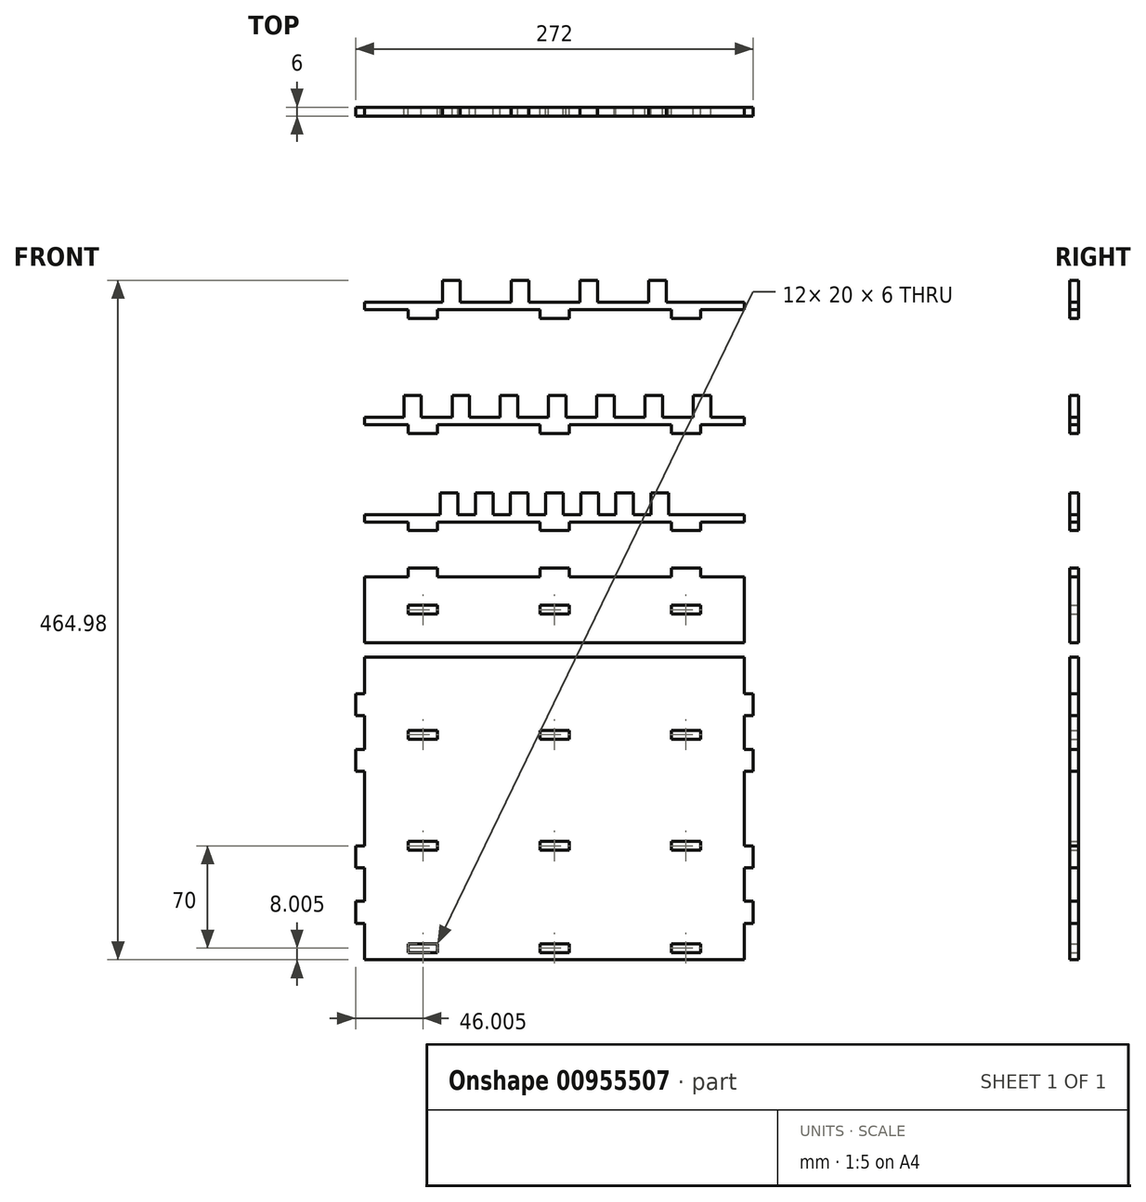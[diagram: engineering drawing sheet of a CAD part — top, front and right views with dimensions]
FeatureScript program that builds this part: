
annotation { "Feature Type Name" : "Feature", "Feature Type Description" : "" }
export const myFeature = defineFeature(function(context is Context, id is Id, definition is map)
    precondition{}
    {
        {
            var Q0;
            Q0=qCreatedBy(makeId("Front.planeOp"),FACE);
            var sketch = newSketch(context, id + "F0", { "sketchPlane" : qUnion([Q0])});
            skLineSegment(sketch, "E0", {"start": v(-47.37, 102.67) * mm, "end": v(-47.37, 117.67) * mm});
            skLineSegment(sketch, "E1", {"start": v(-47.37, 117.67) * mm, "end": v(-35.37, 117.67) * mm});
            skLineSegment(sketch, "E2", {"start": v(-35.37, 117.67) * mm, "end": v(-35.37, 102.67) * mm});
            skLineSegment(sketch, "E3", {"start": v(-35.37, 102.67) * mm, "end": v(-0.37, 102.67) * mm});
            skLineSegment(sketch, "E4.1.0.0", {"start": v(-0.37, 102.67) * mm, "end": v(-0.37, 117.67) * mm});
            skLineSegment(sketch, "E4.1.0.1", {"start": v(-0.37, 117.67) * mm, "end": v(11.63, 117.67) * mm});
            skLineSegment(sketch, "E4.1.0.2", {"start": v(11.63, 117.67) * mm, "end": v(11.63, 102.67) * mm});
            skLineSegment(sketch, "E4.1.0.3", {"start": v(11.63, 102.67) * mm, "end": v(46.63, 102.67) * mm});
            skLineSegment(sketch, "E4.2.0.0", {"start": v(46.63, 102.67) * mm, "end": v(46.63, 117.67) * mm});
            skLineSegment(sketch, "E4.2.0.1", {"start": v(46.63, 117.67) * mm, "end": v(58.63, 117.67) * mm});
            skLineSegment(sketch, "E4.2.0.2", {"start": v(58.63, 117.67) * mm, "end": v(58.63, 102.67) * mm});
            skLineSegment(sketch, "E4.2.0.3", {"start": v(58.63, 102.67) * mm, "end": v(93.63, 102.67) * mm});
            skLineSegment(sketch, "E4.3.0.0", {"start": v(93.63, 102.67) * mm, "end": v(93.63, 117.67) * mm});
            skLineSegment(sketch, "E4.3.0.1", {"start": v(93.63, 117.67) * mm, "end": v(105.63, 117.67) * mm});
            skLineSegment(sketch, "E4.3.0.2", {"start": v(105.63, 117.67) * mm, "end": v(105.63, 102.67) * mm});
            skLineSegment(sketch, "E4.direction1", {"start": v(-47.37, 102.67) * mm, "end": v(-0.37, 102.67) * mm, "construction": true});
            skLineSegment(sketch, "E5", {"start": v(-73.87, 23.95) * mm, "end": v(-73.87, 38.95) * mm});
            skLineSegment(sketch, "E6", {"start": v(-73.87, 38.95) * mm, "end": v(-61.87, 38.95) * mm});
            skLineSegment(sketch, "E7", {"start": v(-61.87, 38.95) * mm, "end": v(-61.87, 23.95) * mm});
            skLineSegment(sketch, "E8", {"start": v(-61.87, 23.95) * mm, "end": v(-40.87, 23.95) * mm});
            skLineSegment(sketch, "E9.1.0.0", {"start": v(-40.87, 23.95) * mm, "end": v(-40.87, 38.95) * mm});
            skLineSegment(sketch, "E9.1.0.1", {"start": v(-40.87, 38.95) * mm, "end": v(-28.87, 38.95) * mm});
            skLineSegment(sketch, "E9.1.0.2", {"start": v(-28.87, 38.95) * mm, "end": v(-28.87, 23.95) * mm});
            skLineSegment(sketch, "E9.1.0.3", {"start": v(-28.87, 23.95) * mm, "end": v(-7.87, 23.95) * mm});
            skLineSegment(sketch, "E9.2.0.0", {"start": v(-7.87, 23.95) * mm, "end": v(-7.87, 38.95) * mm});
            skLineSegment(sketch, "E9.2.0.1", {"start": v(-7.87, 38.95) * mm, "end": v(4.13, 38.95) * mm});
            skLineSegment(sketch, "E9.2.0.2", {"start": v(4.13, 38.95) * mm, "end": v(4.13, 23.95) * mm});
            skLineSegment(sketch, "E9.2.0.3", {"start": v(4.13, 23.95) * mm, "end": v(25.13, 23.95) * mm});
            skLineSegment(sketch, "E9.direction1", {"start": v(-73.87, 23.95) * mm, "end": v(-40.87, 23.95) * mm, "construction": true});
            skLineSegment(sketch, "E10", {"start": v(-47.37, 102.67) * mm, "end": v(-100.87, 102.67) * mm});
            skLineSegment(sketch, "E11", {"start": v(-100.87, 102.67) * mm, "end": v(-100.87, 97.67) * mm});
            skLineSegment(sketch, "E12", {"start": v(-100.87, 97.67) * mm, "end": v(-70.87, 97.67) * mm});
            skLineSegment(sketch, "E13", {"start": v(-73.87, 23.95) * mm, "end": v(-100.87, 23.95) * mm});
            skLineSegment(sketch, "E14", {"start": v(-100.87, 23.95) * mm, "end": v(-100.87, 18.95) * mm});
            skLineSegment(sketch, "E15", {"start": v(-100.87, 18.95) * mm, "end": v(-70.87, 18.95) * mm});
            skLineSegment(sketch, "E16.top", {"start": v(-70.87, 91.67) * mm, "end": v(-50.87, 91.67) * mm});
            skLineSegment(sketch, "E16.left", {"start": v(-70.87, 97.67) * mm, "end": v(-70.87, 91.67) * mm});
            skLineSegment(sketch, "E16.right", {"start": v(-50.87, 97.67) * mm, "end": v(-50.87, 91.67) * mm});
            skLineSegment(sketch, "E17.top", {"start": v(-70.87, 12.95) * mm, "end": v(-50.87, 12.95) * mm});
            skLineSegment(sketch, "E17.left", {"start": v(-70.87, 18.95) * mm, "end": v(-70.87, 12.95) * mm});
            skLineSegment(sketch, "E17.right", {"start": v(-50.87, 18.95) * mm, "end": v(-50.87, 12.95) * mm});
            skLineSegment(sketch, "E18.1.0.0", {"start": v(19.13, 97.67) * mm, "end": v(19.13, 91.67) * mm});
            skLineSegment(sketch, "E18.1.0.1", {"start": v(19.13, 91.67) * mm, "end": v(39.13, 91.67) * mm});
            skLineSegment(sketch, "E18.1.0.2", {"start": v(39.13, 97.67) * mm, "end": v(39.13, 91.67) * mm});
            skLineSegment(sketch, "E18.2.0.0", {"start": v(109.13, 97.67) * mm, "end": v(109.13, 91.67) * mm});
            skLineSegment(sketch, "E18.2.0.1", {"start": v(109.13, 91.67) * mm, "end": v(129.13, 91.67) * mm});
            skLineSegment(sketch, "E18.2.0.2", {"start": v(129.13, 97.67) * mm, "end": v(129.13, 91.67) * mm});
            skLineSegment(sketch, "E18.direction1", {"start": v(-70.87, 91.67) * mm, "end": v(19.13, 91.67) * mm, "construction": true});
            skLineSegment(sketch, "E19.1.0.0", {"start": v(19.13, 18.95) * mm, "end": v(19.13, 12.95) * mm});
            skLineSegment(sketch, "E19.1.0.1", {"start": v(19.13, 12.95) * mm, "end": v(39.13, 12.95) * mm});
            skLineSegment(sketch, "E19.1.0.2", {"start": v(39.13, 18.95) * mm, "end": v(39.13, 12.95) * mm});
            skLineSegment(sketch, "E19.2.0.0", {"start": v(109.13, 18.95) * mm, "end": v(109.13, 12.95) * mm});
            skLineSegment(sketch, "E19.2.0.1", {"start": v(109.13, 12.95) * mm, "end": v(129.13, 12.95) * mm});
            skLineSegment(sketch, "E19.2.0.2", {"start": v(129.13, 18.95) * mm, "end": v(129.13, 12.95) * mm});
            skLineSegment(sketch, "E19.direction1", {"start": v(-70.87, 12.95) * mm, "end": v(19.13, 12.95) * mm, "construction": true});
            skLineSegment(sketch, "E20.trimOffspring", {"start": v(-50.87, 97.67) * mm, "end": v(19.13, 97.67) * mm});
            skLineSegment(sketch, "E21.trimOffspring", {"start": v(39.13, 97.67) * mm, "end": v(109.13, 97.67) * mm});
            skLineSegment(sketch, "E22.trimOffspring", {"start": v(39.13, 18.95) * mm, "end": v(109.13, 18.95) * mm});
            skLineSegment(sketch, "E23.trimOffspring", {"start": v(-50.87, 18.95) * mm, "end": v(19.13, 18.95) * mm});
            skLineSegment(sketch, "E24.bottom", {"start": v(-100.87, -85.27) * mm, "end": v(-70.87, -85.27) * mm});
            skLineSegment(sketch, "E24.top", {"start": v(-100.87, -130.27) * mm, "end": v(159.13, -130.27) * mm});
            skLineSegment(sketch, "E24.left", {"start": v(-100.87, -85.27) * mm, "end": v(-100.87, -130.27) * mm});
            skLineSegment(sketch, "E24.right", {"start": v(159.13, -85.27) * mm, "end": v(159.13, -130.27) * mm});
            skLineSegment(sketch, "E25", {"start": v(-100.87, -107.77) * mm, "end": v(159.13, -107.77) * mm, "construction": true});
            skLineSegment(sketch, "E26.bottom", {"start": v(-70.87, -104.77) * mm, "end": v(-50.87, -104.77) * mm});
            skLineSegment(sketch, "E26.top", {"start": v(-70.87, -110.77) * mm, "end": v(-50.87, -110.77) * mm});
            skLineSegment(sketch, "E26.left", {"start": v(-70.87, -104.77) * mm, "end": v(-70.87, -110.77) * mm});
            skLineSegment(sketch, "E26.right", {"start": v(-50.87, -104.77) * mm, "end": v(-50.87, -110.77) * mm});
            skPoint(sketch, "E26.middle", {"position": v(-60.87, -107.77) * mm});
            skLineSegment(sketch, "E27.1.0.0", {"start": v(19.13, -104.77) * mm, "end": v(39.13, -104.77) * mm});
            skLineSegment(sketch, "E27.1.0.1", {"start": v(19.13, -104.77) * mm, "end": v(19.13, -110.77) * mm});
            skLineSegment(sketch, "E27.1.0.2", {"start": v(19.13, -110.77) * mm, "end": v(39.13, -110.77) * mm});
            skLineSegment(sketch, "E27.1.0.3", {"start": v(39.13, -104.77) * mm, "end": v(39.13, -110.77) * mm});
            skLineSegment(sketch, "E27.2.0.0", {"start": v(109.13, -104.77) * mm, "end": v(129.13, -104.77) * mm});
            skLineSegment(sketch, "E27.2.0.1", {"start": v(109.13, -104.77) * mm, "end": v(109.13, -110.77) * mm});
            skLineSegment(sketch, "E27.2.0.2", {"start": v(109.13, -110.77) * mm, "end": v(129.13, -110.77) * mm});
            skLineSegment(sketch, "E27.2.0.3", {"start": v(129.13, -104.77) * mm, "end": v(129.13, -110.77) * mm});
            skLineSegment(sketch, "E27.direction1", {"start": v(-70.87, -104.77) * mm, "end": v(19.13, -104.77) * mm, "construction": true});
            skLineSegment(sketch, "E28.top", {"start": v(-70.87, -79.27) * mm, "end": v(-50.87, -79.27) * mm});
            skLineSegment(sketch, "E28.left", {"start": v(-70.87, -85.27) * mm, "end": v(-70.87, -79.27) * mm});
            skLineSegment(sketch, "E28.right", {"start": v(-50.87, -85.27) * mm, "end": v(-50.87, -79.27) * mm});
            skLineSegment(sketch, "E29.trimOffspring", {"start": v(-50.87, -85.27) * mm, "end": v(19.13, -85.27) * mm});
            skLineSegment(sketch, "E30.bottom", {"start": v(-100.87, -140.3) * mm, "end": v(159.13, -140.3) * mm});
            skLineSegment(sketch, "E30.top", {"start": v(-100.87, -347.3) * mm, "end": v(159.13, -347.3) * mm});
            skLineSegment(sketch, "E30.left", {"start": v(-100.87, -140.3) * mm, "end": v(-100.87, -165.3) * mm});
            skLineSegment(sketch, "E30.right", {"start": v(159.13, -140.3) * mm, "end": v(159.13, -165.3) * mm});
            skLineSegment(sketch, "E31", {"start": v(-100.87, -193.3) * mm, "end": v(159.13, -193.3) * mm, "construction": true});
            skLineSegment(sketch, "E32", {"start": v(-100.87, -269.3) * mm, "end": v(159.13, -269.3) * mm, "construction": true});
            skLineSegment(sketch, "E33.bottom", {"start": v(-50.87, -196.3) * mm, "end": v(-70.87, -196.3) * mm});
            skLineSegment(sketch, "E33.top", {"start": v(-50.87, -190.3) * mm, "end": v(-70.87, -190.3) * mm});
            skLineSegment(sketch, "E33.left", {"start": v(-50.87, -196.3) * mm, "end": v(-50.87, -190.3) * mm});
            skLineSegment(sketch, "E33.right", {"start": v(-70.87, -196.3) * mm, "end": v(-70.87, -190.3) * mm});
            skPoint(sketch, "E33.middle", {"position": v(-60.87, -193.3) * mm});
            skLineSegment(sketch, "E34.bottom", {"start": v(-50.87, -266.3) * mm, "end": v(-70.87, -266.3) * mm});
            skLineSegment(sketch, "E34.top", {"start": v(-50.87, -272.3) * mm, "end": v(-70.87, -272.3) * mm});
            skLineSegment(sketch, "E34.left", {"start": v(-50.87, -266.3) * mm, "end": v(-50.87, -272.3) * mm});
            skLineSegment(sketch, "E34.right", {"start": v(-70.87, -266.3) * mm, "end": v(-70.87, -272.3) * mm});
            skPoint(sketch, "E34.middle", {"position": v(-60.87, -269.3) * mm});
            skLineSegment(sketch, "E35.1.0.0", {"start": v(39.13, -190.3) * mm, "end": v(19.13, -190.3) * mm});
            skLineSegment(sketch, "E35.1.0.1", {"start": v(19.13, -196.3) * mm, "end": v(19.13, -190.3) * mm});
            skLineSegment(sketch, "E35.1.0.2", {"start": v(39.13, -196.3) * mm, "end": v(19.13, -196.3) * mm});
            skLineSegment(sketch, "E35.1.0.3", {"start": v(39.13, -196.3) * mm, "end": v(39.13, -190.3) * mm});
            skLineSegment(sketch, "E35.2.0.0", {"start": v(129.13, -190.3) * mm, "end": v(109.13, -190.3) * mm});
            skLineSegment(sketch, "E35.2.0.1", {"start": v(109.13, -196.3) * mm, "end": v(109.13, -190.3) * mm});
            skLineSegment(sketch, "E35.2.0.2", {"start": v(129.13, -196.3) * mm, "end": v(109.13, -196.3) * mm});
            skLineSegment(sketch, "E35.2.0.3", {"start": v(129.13, -196.3) * mm, "end": v(129.13, -190.3) * mm});
            skLineSegment(sketch, "E35.direction1", {"start": v(-70.87, -190.3) * mm, "end": v(19.13, -190.3) * mm, "construction": true});
            skLineSegment(sketch, "E36.1.0.0", {"start": v(19.13, -266.3) * mm, "end": v(19.13, -272.3) * mm});
            skLineSegment(sketch, "E36.1.0.1", {"start": v(39.13, -266.3) * mm, "end": v(19.13, -266.3) * mm});
            skLineSegment(sketch, "E36.1.0.2", {"start": v(39.13, -266.3) * mm, "end": v(39.13, -272.3) * mm});
            skLineSegment(sketch, "E36.1.0.3", {"start": v(39.13, -272.3) * mm, "end": v(19.13, -272.3) * mm});
            skLineSegment(sketch, "E36.2.0.0", {"start": v(109.13, -266.3) * mm, "end": v(109.13, -272.3) * mm});
            skLineSegment(sketch, "E36.2.0.1", {"start": v(129.13, -266.3) * mm, "end": v(109.13, -266.3) * mm});
            skLineSegment(sketch, "E36.2.0.2", {"start": v(129.13, -266.3) * mm, "end": v(129.13, -272.3) * mm});
            skLineSegment(sketch, "E36.2.0.3", {"start": v(129.13, -272.3) * mm, "end": v(109.13, -272.3) * mm});
            skLineSegment(sketch, "E36.direction1", {"start": v(-70.87, -272.3) * mm, "end": v(19.13, -272.3) * mm, "construction": true});
            skLineSegment(sketch, "E37.bottom", {"start": v(-100.87, -165.3) * mm, "end": v(-106.87, -165.3) * mm});
            skLineSegment(sketch, "E37.top", {"start": v(-100.87, -180.3) * mm, "end": v(-106.87, -180.3) * mm});
            skLineSegment(sketch, "E37.right", {"start": v(-106.87, -165.3) * mm, "end": v(-106.87, -180.3) * mm});
            skLineSegment(sketch, "E38.0.1.0", {"start": v(-100.87, -203.3) * mm, "end": v(-106.87, -203.3) * mm});
            skLineSegment(sketch, "E38.0.1.2", {"start": v(-100.87, -218.3) * mm, "end": v(-106.87, -218.3) * mm});
            skLineSegment(sketch, "E38.0.1.3", {"start": v(-106.87, -203.3) * mm, "end": v(-106.87, -218.3) * mm});
            skLineSegment(sketch, "E38.1.0.0", {"start": v(165.13, -165.3) * mm, "end": v(159.13, -165.3) * mm});
            skLineSegment(sketch, "E38.1.0.1", {"start": v(165.13, -165.3) * mm, "end": v(165.13, -180.3) * mm});
            skLineSegment(sketch, "E38.1.0.2", {"start": v(165.13, -180.3) * mm, "end": v(159.13, -180.3) * mm});
            skLineSegment(sketch, "E38.1.1.0", {"start": v(165.13, -203.3) * mm, "end": v(159.13, -203.3) * mm});
            skLineSegment(sketch, "E38.1.1.1", {"start": v(165.13, -203.3) * mm, "end": v(165.13, -218.3) * mm});
            skLineSegment(sketch, "E38.1.1.2", {"start": v(165.13, -218.3) * mm, "end": v(159.13, -218.3) * mm});
            skLineSegment(sketch, "E38.direction1", {"start": v(-106.87, -165.3) * mm, "end": v(159.13, -165.3) * mm, "construction": true});
            skLineSegment(sketch, "E38.direction2", {"start": v(-106.87, -165.3) * mm, "end": v(-106.87, -203.3) * mm, "construction": true});
            skLineSegment(sketch, "E39.trimOffspring", {"start": v(-100.87, -218.3) * mm, "end": v(-100.87, -267.3) * mm});
            skLineSegment(sketch, "E40.trimOffspring", {"start": v(-100.87, -267.3) * mm, "end": v(-100.87, -269.3) * mm});
            skLineSegment(sketch, "E41.trimOffspring", {"start": v(159.13, -180.3) * mm, "end": v(159.13, -203.3) * mm});
            skLineSegment(sketch, "E42.trimOffspring", {"start": v(159.13, -267.3) * mm, "end": v(159.13, -269.3) * mm});
            skLineSegment(sketch, "E43.trimOffspring", {"start": v(159.13, -218.3) * mm, "end": v(159.13, -267.3) * mm});
            skLineSegment(sketch, "E44.trimOffspring", {"start": v(-100.87, -180.3) * mm, "end": v(-100.87, -203.3) * mm});
            skLineSegment(sketch, "E45.0.3.0", {"start": v(25.13, 23.95) * mm, "end": v(25.13, 38.95) * mm});
            skLineSegment(sketch, "E45.3.3.0", {"start": v(25.13, 38.95) * mm, "end": v(37.13, 38.95) * mm});
            skLineSegment(sketch, "E45.6.3.0", {"start": v(37.13, 38.95) * mm, "end": v(37.13, 23.95) * mm});
            skLineSegment(sketch, "E45.9.3.0", {"start": v(37.13, 23.95) * mm, "end": v(58.13, 23.95) * mm});
            skLineSegment(sketch, "E45.0.4.0", {"start": v(58.13, 23.95) * mm, "end": v(58.13, 38.95) * mm});
            skLineSegment(sketch, "E45.3.4.0", {"start": v(58.13, 38.95) * mm, "end": v(70.13, 38.95) * mm});
            skLineSegment(sketch, "E45.6.4.0", {"start": v(70.13, 38.95) * mm, "end": v(70.13, 23.95) * mm});
            skLineSegment(sketch, "E45.9.4.0", {"start": v(70.13, 23.95) * mm, "end": v(91.13, 23.95) * mm});
            skLineSegment(sketch, "E45.0.5.0", {"start": v(91.13, 23.95) * mm, "end": v(91.13, 38.95) * mm});
            skLineSegment(sketch, "E45.3.5.0", {"start": v(91.13, 38.95) * mm, "end": v(103.13, 38.95) * mm});
            skLineSegment(sketch, "E45.6.5.0", {"start": v(103.13, 38.95) * mm, "end": v(103.13, 23.95) * mm});
            skLineSegment(sketch, "E45.9.5.0", {"start": v(103.13, 23.95) * mm, "end": v(124.13, 23.95) * mm});
            skLineSegment(sketch, "E45.0.6.0", {"start": v(124.13, 23.95) * mm, "end": v(124.13, 38.95) * mm});
            skLineSegment(sketch, "E45.3.6.0", {"start": v(124.13, 38.95) * mm, "end": v(136.13, 38.95) * mm});
            skLineSegment(sketch, "E45.6.6.0", {"start": v(136.13, 38.95) * mm, "end": v(136.13, 23.95) * mm});
            skLineSegment(sketch, "E46", {"start": v(-48.87, -42.65) * mm, "end": v(-48.87, -27.65) * mm});
            skLineSegment(sketch, "E47", {"start": v(-48.87, -27.65) * mm, "end": v(-36.87, -27.65) * mm});
            skLineSegment(sketch, "E48", {"start": v(-36.87, -27.65) * mm, "end": v(-36.87, -42.65) * mm});
            skLineSegment(sketch, "E49", {"start": v(-36.87, -42.65) * mm, "end": v(-24.87, -42.65) * mm});
            skLineSegment(sketch, "E50.1.0.0", {"start": v(-24.87, -42.65) * mm, "end": v(-24.87, -27.65) * mm});
            skLineSegment(sketch, "E50.1.0.1", {"start": v(-24.87, -27.65) * mm, "end": v(-12.87, -27.65) * mm});
            skLineSegment(sketch, "E50.1.0.2", {"start": v(-12.87, -27.65) * mm, "end": v(-12.87, -42.65) * mm});
            skLineSegment(sketch, "E50.1.0.3", {"start": v(-12.87, -42.65) * mm, "end": v(-0.87, -42.65) * mm});
            skLineSegment(sketch, "E50.2.0.0", {"start": v(-0.87, -42.65) * mm, "end": v(-0.87, -27.65) * mm});
            skLineSegment(sketch, "E50.2.0.1", {"start": v(-0.87, -27.65) * mm, "end": v(11.13, -27.65) * mm});
            skLineSegment(sketch, "E50.2.0.2", {"start": v(11.13, -27.65) * mm, "end": v(11.13, -42.65) * mm});
            skLineSegment(sketch, "E50.2.0.3", {"start": v(11.13, -42.65) * mm, "end": v(23.13, -42.65) * mm});
            skLineSegment(sketch, "E50.direction1", {"start": v(-48.87, -42.65) * mm, "end": v(-24.87, -42.65) * mm, "construction": true});
            skLineSegment(sketch, "E51", {"start": v(-48.87, -42.65) * mm, "end": v(-100.87, -42.65) * mm});
            skLineSegment(sketch, "E52", {"start": v(-100.87, -42.65) * mm, "end": v(-100.87, -47.65) * mm});
            skLineSegment(sketch, "E53", {"start": v(-100.87, -47.65) * mm, "end": v(-70.87, -47.65) * mm});
            skLineSegment(sketch, "E54.top", {"start": v(-70.87, -53.65) * mm, "end": v(-50.87, -53.65) * mm});
            skLineSegment(sketch, "E54.left", {"start": v(-70.87, -47.65) * mm, "end": v(-70.87, -53.65) * mm});
            skLineSegment(sketch, "E54.right", {"start": v(-50.87, -47.65) * mm, "end": v(-50.87, -53.65) * mm});
            skLineSegment(sketch, "E55.1.0.0", {"start": v(19.13, -47.65) * mm, "end": v(19.13, -53.65) * mm});
            skLineSegment(sketch, "E55.1.0.1", {"start": v(19.13, -53.65) * mm, "end": v(39.13, -53.65) * mm});
            skLineSegment(sketch, "E55.1.0.2", {"start": v(39.13, -47.65) * mm, "end": v(39.13, -53.65) * mm});
            skLineSegment(sketch, "E55.2.0.0", {"start": v(109.13, -47.65) * mm, "end": v(109.13, -53.65) * mm});
            skLineSegment(sketch, "E55.2.0.1", {"start": v(109.13, -53.65) * mm, "end": v(129.13, -53.65) * mm});
            skLineSegment(sketch, "E55.2.0.2", {"start": v(129.13, -47.65) * mm, "end": v(129.13, -53.65) * mm});
            skLineSegment(sketch, "E55.direction1", {"start": v(-70.87, -53.65) * mm, "end": v(19.13, -53.65) * mm, "construction": true});
            skLineSegment(sketch, "E56.trimOffspring", {"start": v(39.13, -47.65) * mm, "end": v(109.13, -47.65) * mm});
            skLineSegment(sketch, "E57.trimOffspring", {"start": v(-50.87, -47.65) * mm, "end": v(19.13, -47.65) * mm});
            skLineSegment(sketch, "E58.0.3.0", {"start": v(23.13, -42.65) * mm, "end": v(23.13, -27.65) * mm});
            skLineSegment(sketch, "E58.3.3.0", {"start": v(23.13, -27.65) * mm, "end": v(35.13, -27.65) * mm});
            skLineSegment(sketch, "E58.6.3.0", {"start": v(35.13, -27.65) * mm, "end": v(35.13, -42.65) * mm});
            skLineSegment(sketch, "E58.9.3.0", {"start": v(35.13, -42.65) * mm, "end": v(47.13, -42.65) * mm});
            skLineSegment(sketch, "E58.0.4.0", {"start": v(47.13, -42.65) * mm, "end": v(47.13, -27.65) * mm});
            skLineSegment(sketch, "E58.3.4.0", {"start": v(47.13, -27.65) * mm, "end": v(59.13, -27.65) * mm});
            skLineSegment(sketch, "E58.6.4.0", {"start": v(59.13, -27.65) * mm, "end": v(59.13, -42.65) * mm});
            skLineSegment(sketch, "E58.9.4.0", {"start": v(59.13, -42.65) * mm, "end": v(71.13, -42.65) * mm});
            skLineSegment(sketch, "E58.0.5.0", {"start": v(71.13, -42.65) * mm, "end": v(71.13, -27.65) * mm});
            skLineSegment(sketch, "E58.3.5.0", {"start": v(71.13, -27.65) * mm, "end": v(83.13, -27.65) * mm});
            skLineSegment(sketch, "E58.6.5.0", {"start": v(83.13, -27.65) * mm, "end": v(83.13, -42.65) * mm});
            skLineSegment(sketch, "E58.9.5.0", {"start": v(83.13, -42.65) * mm, "end": v(95.13, -42.65) * mm});
            skLineSegment(sketch, "E58.0.6.0", {"start": v(95.13, -42.65) * mm, "end": v(95.13, -27.65) * mm});
            skLineSegment(sketch, "E58.3.6.0", {"start": v(95.13, -27.65) * mm, "end": v(107.13, -27.65) * mm});
            skLineSegment(sketch, "E58.6.6.0", {"start": v(107.13, -27.65) * mm, "end": v(107.13, -42.65) * mm});
            skLineSegment(sketch, "E59", {"start": v(129.13, 18.95) * mm, "end": v(159.13, 18.95) * mm});
            skLineSegment(sketch, "E60", {"start": v(159.13, 18.95) * mm, "end": v(159.13, 23.95) * mm});
            skLineSegment(sketch, "E61", {"start": v(105.63, 102.67) * mm, "end": v(159.13, 102.67) * mm});
            skLineSegment(sketch, "E62", {"start": v(159.13, 102.67) * mm, "end": v(159.13, 97.67) * mm});
            skLineSegment(sketch, "E63", {"start": v(159.13, 97.67) * mm, "end": v(129.13, 97.67) * mm});
            skLineSegment(sketch, "E64", {"start": v(129.13, -47.65) * mm, "end": v(159.13, -47.65) * mm});
            skLineSegment(sketch, "E65", {"start": v(159.13, -47.65) * mm, "end": v(159.13, -42.65) * mm});
            skPoint(sketch, "E58.9.6.0.end.orphan", {"position": v(159.13, -42.65) * mm});
            skLineSegment(sketch, "E66", {"start": v(107.13, -42.65) * mm, "end": v(159.13, -42.65) * mm});
            skLineSegment(sketch, "E67", {"start": v(136.13, 23.95) * mm, "end": v(159.13, 23.95) * mm});
            skLineSegment(sketch, "E68.1.0.0", {"start": v(19.13, -85.27) * mm, "end": v(19.13, -79.27) * mm});
            skLineSegment(sketch, "E68.1.0.1", {"start": v(19.13, -79.27) * mm, "end": v(39.13, -79.27) * mm});
            skLineSegment(sketch, "E68.1.0.2", {"start": v(39.13, -85.27) * mm, "end": v(39.13, -79.27) * mm});
            skLineSegment(sketch, "E68.2.0.0", {"start": v(109.13, -85.27) * mm, "end": v(109.13, -79.27) * mm});
            skLineSegment(sketch, "E68.2.0.1", {"start": v(109.13, -79.27) * mm, "end": v(129.13, -79.27) * mm});
            skLineSegment(sketch, "E68.2.0.2", {"start": v(129.13, -85.27) * mm, "end": v(129.13, -79.27) * mm});
            skLineSegment(sketch, "E68.direction1", {"start": v(-70.87, -85.27) * mm, "end": v(19.13, -85.27) * mm, "construction": true});
            skLineSegment(sketch, "E69.trimOffspring", {"start": v(39.13, -85.27) * mm, "end": v(109.13, -85.27) * mm});
            skLineSegment(sketch, "E70.trimOffspring", {"start": v(129.13, -85.27) * mm, "end": v(159.13, -85.27) * mm});
            skLineSegment(sketch, "E71", {"start": v(-100.87, -339.3) * mm, "end": v(151.56, -339.3) * mm, "construction": true});
            skLineSegment(sketch, "E72.bottom", {"start": v(-70.87, -336.3) * mm, "end": v(-50.87, -336.3) * mm});
            skLineSegment(sketch, "E72.top", {"start": v(-70.87, -342.3) * mm, "end": v(-50.87, -342.3) * mm});
            skLineSegment(sketch, "E72.left", {"start": v(-70.87, -336.3) * mm, "end": v(-70.87, -342.3) * mm});
            skLineSegment(sketch, "E72.right", {"start": v(-50.87, -336.3) * mm, "end": v(-50.87, -342.3) * mm});
            skPoint(sketch, "E72.middle", {"position": v(-60.87, -339.3) * mm});
            skLineSegment(sketch, "E73.1.0.0", {"start": v(19.13, -336.3) * mm, "end": v(39.13, -336.3) * mm});
            skLineSegment(sketch, "E73.1.0.1", {"start": v(19.13, -336.3) * mm, "end": v(19.13, -342.3) * mm});
            skLineSegment(sketch, "E73.1.0.2", {"start": v(19.13, -342.3) * mm, "end": v(39.13, -342.3) * mm});
            skLineSegment(sketch, "E73.1.0.3", {"start": v(39.13, -336.3) * mm, "end": v(39.13, -342.3) * mm});
            skLineSegment(sketch, "E73.2.0.0", {"start": v(109.13, -336.3) * mm, "end": v(129.13, -336.3) * mm});
            skLineSegment(sketch, "E73.2.0.1", {"start": v(109.13, -336.3) * mm, "end": v(109.13, -342.3) * mm});
            skLineSegment(sketch, "E73.2.0.2", {"start": v(109.13, -342.3) * mm, "end": v(129.13, -342.3) * mm});
            skLineSegment(sketch, "E73.2.0.3", {"start": v(129.13, -336.3) * mm, "end": v(129.13, -342.3) * mm});
            skLineSegment(sketch, "E73.direction1", {"start": v(-70.87, -336.3) * mm, "end": v(19.13, -336.3) * mm, "construction": true});
            skLineSegment(sketch, "E74.bottom", {"start": v(-100.87, -269.3) * mm, "end": v(-106.87, -269.3) * mm});
            skLineSegment(sketch, "E74.top", {"start": v(-100.87, -284.3) * mm, "end": v(-106.87, -284.3) * mm});
            skLineSegment(sketch, "E74.right", {"start": v(-106.87, -269.3) * mm, "end": v(-106.87, -284.3) * mm});
            skLineSegment(sketch, "E75.0.1.0", {"start": v(-106.87, -307.3) * mm, "end": v(-106.87, -322.3) * mm});
            skLineSegment(sketch, "E75.0.1.1", {"start": v(-100.87, -307.3) * mm, "end": v(-106.87, -307.3) * mm});
            skLineSegment(sketch, "E75.0.1.3", {"start": v(-100.87, -322.3) * mm, "end": v(-106.87, -322.3) * mm});
            skLineSegment(sketch, "E75.1.0.1", {"start": v(165.13, -269.3) * mm, "end": v(159.13, -269.3) * mm});
            skLineSegment(sketch, "E75.1.0.2", {"start": v(165.13, -269.3) * mm, "end": v(165.13, -284.3) * mm});
            skLineSegment(sketch, "E75.1.0.3", {"start": v(165.13, -284.3) * mm, "end": v(159.13, -284.3) * mm});
            skLineSegment(sketch, "E75.1.1.1", {"start": v(165.13, -307.3) * mm, "end": v(159.13, -307.3) * mm});
            skLineSegment(sketch, "E75.1.1.2", {"start": v(165.13, -307.3) * mm, "end": v(165.13, -322.3) * mm});
            skLineSegment(sketch, "E75.1.1.3", {"start": v(165.13, -322.3) * mm, "end": v(159.13, -322.3) * mm});
            skLineSegment(sketch, "E75.direction1", {"start": v(-106.87, -284.3) * mm, "end": v(159.13, -284.3) * mm, "construction": true});
            skLineSegment(sketch, "E75.direction2", {"start": v(-106.87, -284.3) * mm, "end": v(-106.87, -322.3) * mm, "construction": true});
            skLineSegment(sketch, "E76.trimOffspring", {"start": v(159.13, -284.3) * mm, "end": v(159.13, -307.3) * mm});
            skLineSegment(sketch, "E77.trimOffspring", {"start": v(159.13, -322.3) * mm, "end": v(159.13, -347.3) * mm});
            skLineSegment(sketch, "E78.trimOffspring", {"start": v(-100.87, -322.3) * mm, "end": v(-100.87, -347.3) * mm});
            skLineSegment(sketch, "E79.trimOffspring", {"start": v(-100.87, -284.3) * mm, "end": v(-100.87, -307.3) * mm});
            skSolve(sketch);
        }
        {
            var Q0;
            Q0=makeQuery(id+"F0.imprint","IMPRINT",FACE,{"disambiguationData":[TD([[makeQuery(id+"F0.imprint","IMPRINT",EDGE,{"derivedFrom":sQuery(id+"F0.wireOp",EDGE,"E30.bottom")}),-1.0]])]});
            extrude(context, id + "F1", {"entities" : qUnion([Q0]), "depth" : 6 * mm, "offsetDistance" : 25 * mm});
        }
        {
            var Q0;
            Q0=makeQuery(id+"F0.imprint","IMPRINT",FACE,{"disambiguationData":[TD([[makeQuery(id+"F0.imprint","IMPRINT",EDGE,{"derivedFrom":sQuery(id+"F0.wireOp",EDGE,"E24.bottom")}),-1.0]])]});
            extrude(context, id + "F2", {"entities" : qUnion([Q0]), "depth" : 6 * mm, "offsetDistance" : 25 * mm});
        }
        {
            var Q0;
            Q0=makeQuery(id+"F0.imprint","IMPRINT",FACE,{"disambiguationData":[TD([[makeQuery(id+"F0.imprint","IMPRINT",EDGE,{"derivedFrom":sQuery(id+"F0.wireOp",EDGE,"E0")}),-1.0]])]});
            extrude(context, id + "F3", {"entities" : qUnion([Q0]), "depth" : 6 * mm, "offsetDistance" : 25 * mm});
        }
        {
            var Q0;
            Q0=makeQuery(id+"F0.imprint","IMPRINT",FACE,{"disambiguationData":[TD([[makeQuery(id+"F0.imprint","IMPRINT",EDGE,{"derivedFrom":sQuery(id+"F0.wireOp",EDGE,"E5")}),-1.0]])]});
            var Q1;
            Q1=makeQuery(id+"F0.imprint","IMPRINT",FACE,{"disambiguationData":[TD([[makeQuery(id+"F0.imprint","IMPRINT",EDGE,{"derivedFrom":sQuery(id+"F0.wireOp",EDGE,"E46")}),-1.0]])]});
            extrude(context, id + "F4", {"entities" : qUnion([Q0, Q1]), "depth" : 6 * mm, "offsetDistance" : 25 * mm});
        }
    });
